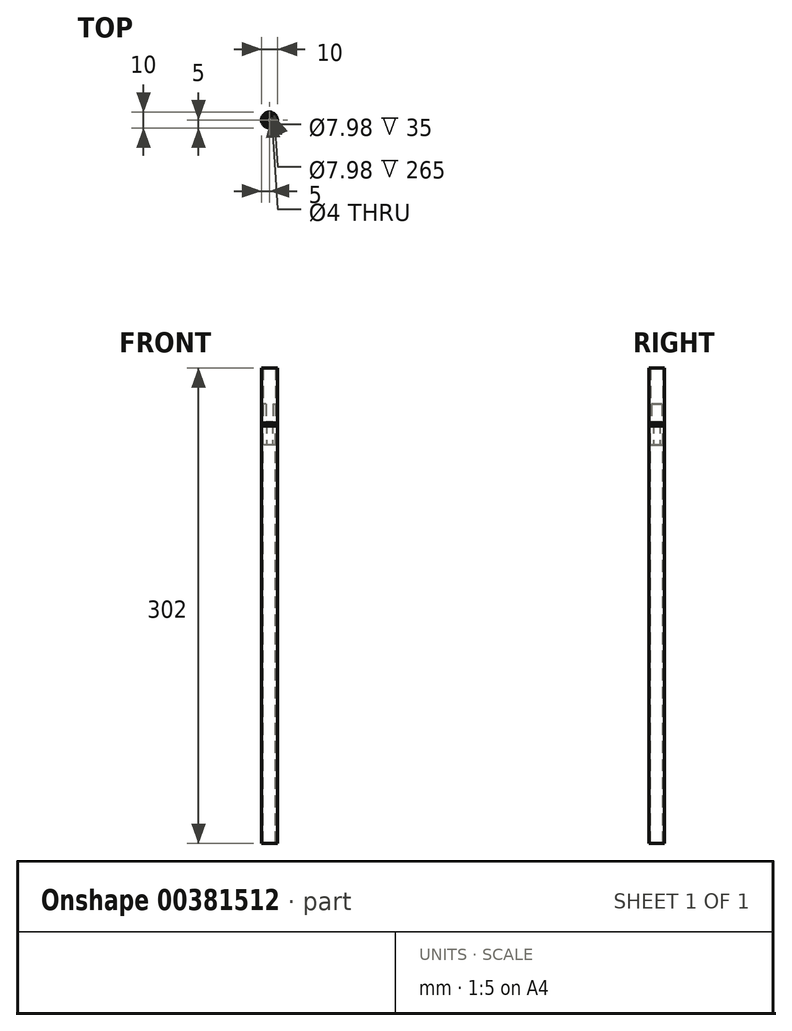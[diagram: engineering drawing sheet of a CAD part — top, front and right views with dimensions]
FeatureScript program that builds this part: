
annotation { "Feature Type Name" : "Feature", "Feature Type Description" : "" }
export const myFeature = defineFeature(function(context is Context, id is Id, definition is map)
    precondition{}
    {
        {
            var Q0;
            Q0=qCreatedBy(makeId("Top.planeOp"),FACE);
            var sketch = newSketch(context, id + "F0", { "sketchPlane" : qUnion([Q0])});
            skCircle(sketch, "E0", {"center": v(0, 0) * mm, "radius": 4 * mm});
            skCircle(sketch, "E1", {"center": v(0, 0) * mm, "radius": 2 * mm});
            skCircle(sketch, "E2", {"center": v(0, 0) * mm, "radius": 5 * mm});
            skSolve(sketch);
        }
        {
            var Q0;
            Q0=makeQuery(id+"F0.imprint","IMPRINT",FACE,{"disambiguationData":[TD([[makeQuery(id+"F0.imprint","IMPRINT",EDGE,{"derivedFrom":sQuery(id+"F0.wireOp",EDGE,"E0")}),1.0]])]});
            extrude(context, id + "F1", {"entities" : qUnion([Q0]), "depth" : 14 * mm});
        }
        {
            var Q0;
            Q0=makeQuery(id+"F1.opExtrude","CAP_FACE",FACE,{"disambiguationData":[OSD([sQuery(id+"F0.wireOp",EDGE,"E0"),sQuery(id+"F0.wireOp",EDGE,"E1")])],"isStart":false});
            var sketch = newSketch(context, id + "F2", { "sketchPlane" : qUnion([Q0])});
            skCircle(sketch, "E3.0", {"center": v(0, 0) * mm, "radius": 4 * mm});
            skCircle(sketch, "E4.0", {"center": v(0, 0) * mm, "radius": 2 * mm});
            skLineSegment(sketch, "E5", {"start": v(0, -4) * mm, "end": v(0, 0) * mm, "construction": true});
            skLineSegment(sketch, "E6", {"start": v(0, 4) * mm, "end": v(0, 0) * mm, "construction": true});
            skLineSegment(sketch, "E7", {"start": v(4, 0) * mm, "end": v(0, 0) * mm, "construction": true});
            skLineSegment(sketch, "E8", {"start": v(-4, 0) * mm, "end": v(0, 0) * mm, "construction": true});
            skLineSegment(sketch, "E9.bottom", {"start": v(-2.1, 5) * mm, "end": v(2.1, 5) * mm});
            skLineSegment(sketch, "E9.top", {"start": v(-2.1, -5) * mm, "end": v(2.1, -5) * mm});
            skLineSegment(sketch, "E9.left", {"start": v(-2.1, 5) * mm, "end": v(-2.1, -5) * mm});
            skLineSegment(sketch, "E9.right", {"start": v(2.1, 5) * mm, "end": v(2.1, -5) * mm});
            skSolve(sketch);
        }
        {
            var Q0;
            {var subQ5=sQuery(id+"F2.wireOp",EDGE,"E9.bottom");Q0=makeQuery(id+"F2.imprint","IMPRINT",FACE,{"disambiguationData":[TD([[makeQuery(id+"F2.imprint","IMPRINT",EDGE,{"derivedFrom":subQ5}),-1.0]])]});}
            var Q1;
            {var subQ0=sQuery(id+"F2.wireOp",EDGE,"E9.left");var subQ1=sQuery(id+"F2.wireOp",EDGE,"E3.0");var subQ2=makeQuery(id+"F2.imprint","INTERSECT",VERTEX,{"disambiguationData":[OD(0.0)],"derivedFrom":[subQ1,subQ0]});Q1=makeQuery(id+"F2.imprint","IMPRINT",FACE,{"disambiguationData":[TD([[makeQuery(id+"F2.imprint","IMPRINT",EDGE,{"disambiguationData":[TD([[subQ2,1.0]])],"derivedFrom":subQ1}),1.0]])]});}
            var Q2;
            {var subQ0=sQuery(id+"F2.wireOp",EDGE,"E9.left");var subQ1=sQuery(id+"F2.wireOp",EDGE,"E4.0");var subQ2=makeQuery(id+"F2.imprint","INTERSECT",VERTEX,{"disambiguationData":[OD(0.0)],"derivedFrom":[subQ1,subQ0]});Q2=makeQuery(id+"F2.imprint","IMPRINT",FACE,{"disambiguationData":[TD([[makeQuery(id+"F2.imprint","IMPRINT",EDGE,{"disambiguationData":[TD([[subQ2,1.0]])],"derivedFrom":subQ1}),1.0]])]});}
            var Q3;
            {var subQ0=sQuery(id+"F2.wireOp",EDGE,"E9.left");var subQ1=sQuery(id+"F2.wireOp",EDGE,"E3.0");var subQ2=makeQuery(id+"F2.imprint","INTERSECT",VERTEX,{"disambiguationData":[OD(1.0)],"derivedFrom":[subQ1,subQ0]});Q3=makeQuery(id+"F2.imprint","IMPRINT",FACE,{"disambiguationData":[TD([[makeQuery(id+"F2.imprint","IMPRINT",EDGE,{"disambiguationData":[TD([[subQ2,-1.0]])],"derivedFrom":subQ1}),1.0]])]});}
            var Q4;
            {var subQ5=sQuery(id+"F2.wireOp",EDGE,"E9.top");Q4=makeQuery(id+"F2.imprint","IMPRINT",FACE,{"disambiguationData":[TD([[makeQuery(id+"F2.imprint","IMPRINT",EDGE,{"derivedFrom":subQ5}),1.0]])]});}
            extrude(context, id + "F3", {"entities" : qUnion([Q0, Q1, Q2, Q3, Q4]), "operationType" : NewBodyOperationType.REMOVE, "oppositeDirection" : true, "depth" : 11.2 * mm});
        }
        {
            var Q0;
            Q0=makeQuery(id+"F0.imprint","IMPRINT",FACE,{"disambiguationData":[TD([[makeQuery(id+"F0.imprint","IMPRINT",EDGE,{"derivedFrom":sQuery(id+"F0.wireOp",EDGE,"E0")}),-1.0]])]});
            extrude(context, id + "F4", {"entities" : qUnion([Q0]), "operationType" : NewBodyOperationType.ADD, "depth" : 2 * mm});
        }
        {
            var Q0;
            Q0=makeQuery(id+"F0.imprint","IMPRINT",FACE,{"disambiguationData":[TD([[makeQuery(id+"F0.imprint","IMPRINT",EDGE,{"derivedFrom":sQuery(id+"F0.wireOp",EDGE,"E0")}),1.0]])]});
            extrude(context, id + "F5", {"entities" : qUnion([Q0]), "operationType" : NewBodyOperationType.ADD, "oppositeDirection" : true, "depth" : 12 * mm});
        }
        {
            var Q0;
            Q0=makeQuery(id+"F4.opExtrude","CAP_FACE",FACE,{"disambiguationData":[OSD([sQuery(id+"F0.wireOp",EDGE,"E0"),sQuery(id+"F0.wireOp",EDGE,"E2")])],"isStart":false});
            extrude(context, id + "F6", {"entities" : qUnion([Q0]), "depth" : 35 * mm});
        }
        {
            var Q0;
            {var subQ0=sQuery(id+"F0.wireOp",EDGE,"E0");Q0=makeQuery(id+"F4.boolean.opBoolean","MERGE",FACE,{"derivedFrom":[makeQuery(id+"F1.opExtrude","CAP_FACE",FACE,{"disambiguationData":[OSD([subQ0,sQuery(id+"F0.wireOp",EDGE,"E1")])],"isStart":true}),makeQuery(id+"F4.opExtrude","CAP_FACE",FACE,{"disambiguationData":[OSD([subQ0,sQuery(id+"F0.wireOp",EDGE,"E2")])],"isStart":true})]});}
            extrude(context, id + "F7", {"entities" : qUnion([Q0]), "depth" : 265 * mm});
        }
    });
